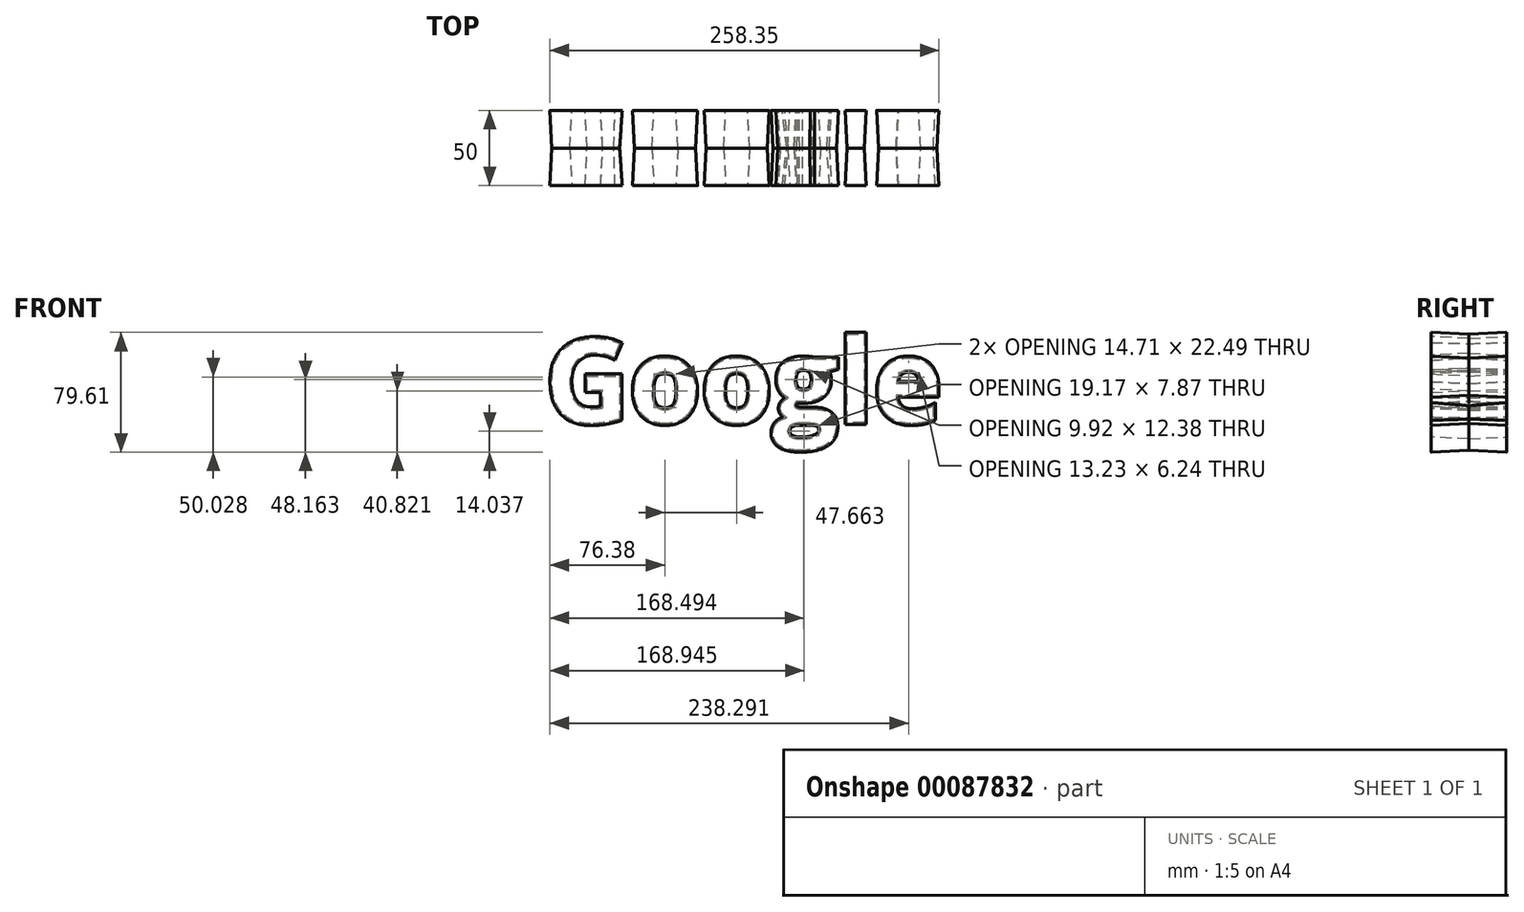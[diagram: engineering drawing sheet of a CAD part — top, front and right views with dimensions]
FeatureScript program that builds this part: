
annotation { "Feature Type Name" : "Feature", "Feature Type Description" : "" }
export const myFeature = defineFeature(function(context is Context, id is Id, definition is map)
    precondition{}
    {
        {
            var Q0;
            Q0=qCreatedBy(makeId("Front.planeOp"),FACE);
            var sketch = newSketch(context, id + "F0", { "sketchPlane" : qUnion([Q0])});
            skText(sketch, "E0", { "text": "Google", "fontName": "OpenSans-Bold.ttf"});
            const initialGuessF0  = {"E0": [-0.17057, -0.03661, 1, 0, 0.05542]};
            skSetInitialGuess(sketch, initialGuessF0);
            skSolve(sketch);
        }
        {
            var Q0;
            Q0 = qSketchRegion(id + "F0", true);
            extrude(context, id + "F1", {"entities" : qUnion([Q0]), "endBound" : BoundingType.SYMMETRIC, "depth" : 50 * mm, "hasDraft" : true, "draftAngle" : 3 * degree});
        }
    });
